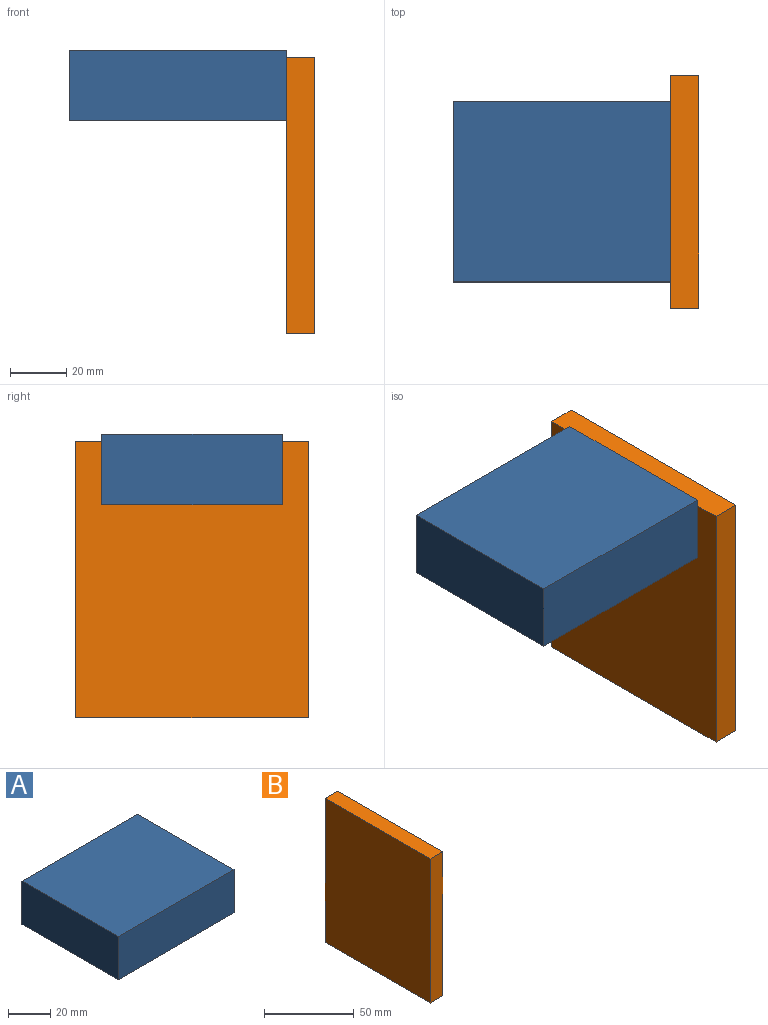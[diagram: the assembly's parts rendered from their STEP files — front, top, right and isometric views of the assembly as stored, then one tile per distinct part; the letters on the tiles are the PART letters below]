
ASSEMBLY  parts=2 mates=1
PART A: 6 faces, bbox 77.4x64.3x25 mm
  f0: plane 64.25x25mm, normal (-1,0,0), area 1606.3mm2, adj f1,f3,f4,f5
  f1: plane 77.44x25mm, normal (0,-1,0), area 1936mm2, adj f0,f2,f4,f5
  f2: plane 64.25x25mm, normal (1,0,0), area 1606.3mm2, adj f1,f3,f4,f5
  f3: plane 77.44x25mm, normal (0,1,0), area 1936mm2, adj f0,f2,f4,f5
  f4: plane 77.44x64.25mm, normal (0,0,1), area 4975.7mm2, adj f0,f1,f2,f3
  f5: plane 77.44x64.25mm, normal (0,0,-1), area 4975.7mm2, adj f0,f1,f2,f3
PART B: 6 faces, bbox 10x82.9x98.3 mm
  f0: plane 98.32x10mm, normal (0,-1,0), area 983.2mm2, adj f1,f3,f4,f5
  f1: plane 82.94x10mm, normal (0,0,-1), area 829.4mm2, adj f0,f2,f4,f5
  f2: plane 98.32x10mm, normal (0,1,0), area 983.2mm2, adj f1,f3,f4,f5
  f3: plane 82.94x10mm, normal (0,0,1), area 829.4mm2, adj f0,f2,f4,f5
  f4: plane 98.32x82.94mm, normal (1,0,0), area 8154.7mm2, adj f0,f1,f2,f3
  f5: plane 98.32x82.94mm, normal (-1,0,0), area 8154.7mm2, adj f0,f1,f2,f3
PLACE A t=(-50.64,-10.15,6.82)mm
PLACE B rot(axis=(0,0,1),180deg) t=(-1.72,-16.25,-19.84)mm
MATE fastened B.f4 <-> A.f2  axis (-1,0,0) through (-11.72,-16.25,19.32)mm
